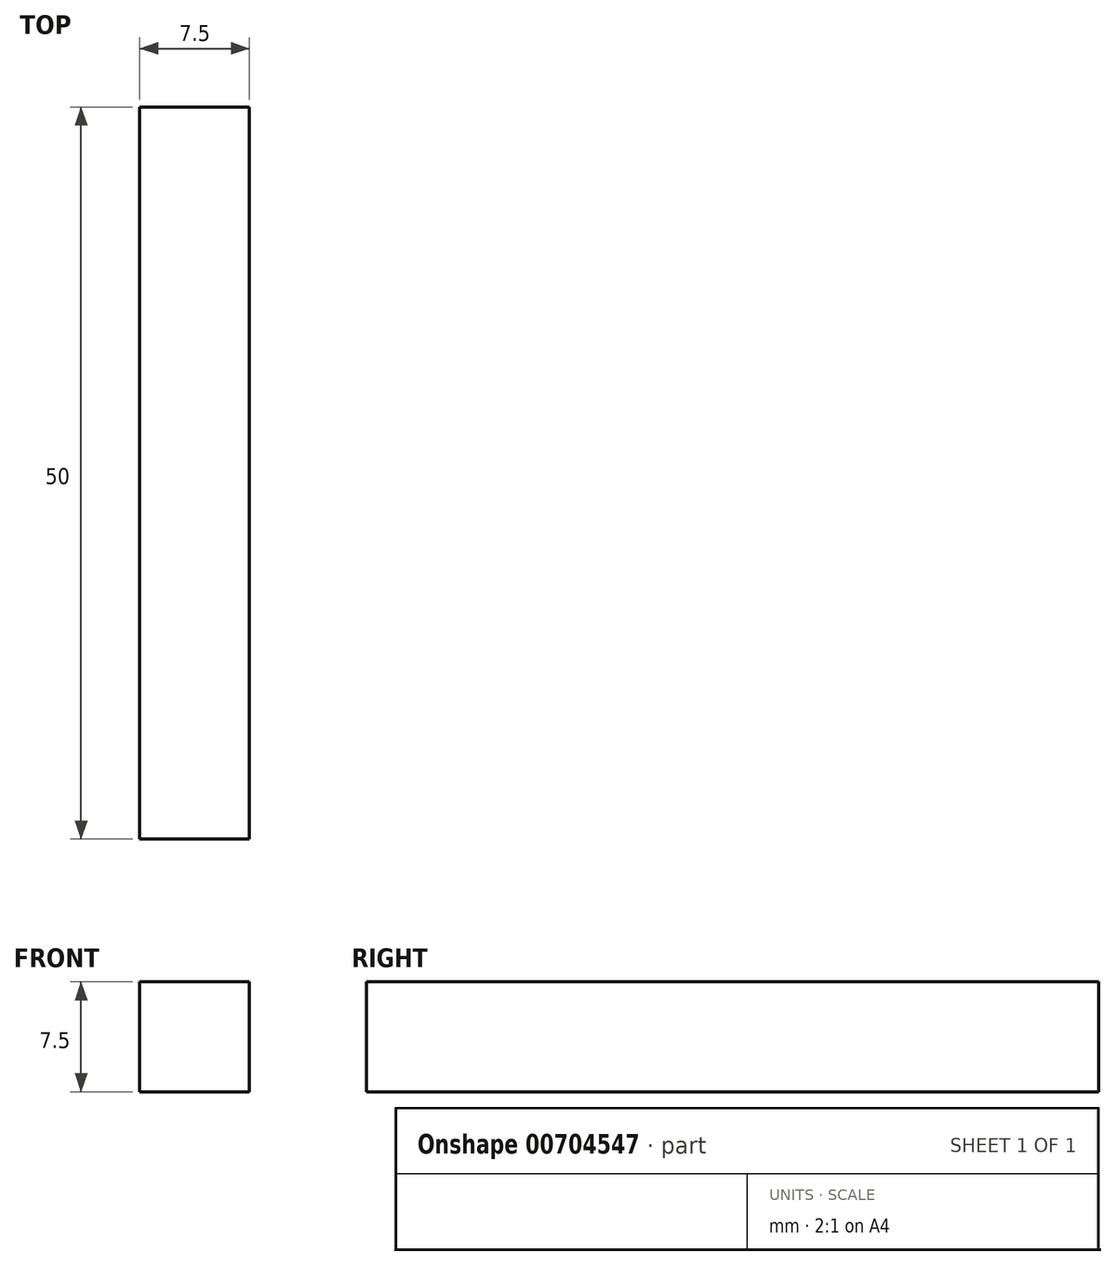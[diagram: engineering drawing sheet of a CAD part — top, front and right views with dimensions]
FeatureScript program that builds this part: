
annotation { "Feature Type Name" : "Feature", "Feature Type Description" : "" }
export const myFeature = defineFeature(function(context is Context, id is Id, definition is map)
    precondition{}
    {
        {
            var Q0;
            Q0=qCreatedBy(makeId("Front.planeOp"),FACE);
            var sketch = newSketch(context, id + "F0", { "sketchPlane" : qUnion([Q0])});
            skLineSegment(sketch, "E0.bottom", {"start": v(3.75, 3.75) * mm, "end": v(-3.75, 3.75) * mm});
            skLineSegment(sketch, "E0.top", {"start": v(3.75, -3.75) * mm, "end": v(-3.75, -3.75) * mm});
            skLineSegment(sketch, "E0.left", {"start": v(3.75, 3.75) * mm, "end": v(3.75, -3.75) * mm});
            skLineSegment(sketch, "E0.right", {"start": v(-3.75, 3.75) * mm, "end": v(-3.75, -3.75) * mm});
            skPoint(sketch, "E0.middle", {"position": v(0, 0) * mm});
            skSolve(sketch);
        }
        {
            var Q0;
            Q0 = qSketchRegion(id + "F0", true);
            extrude(context, id + "F1", {"entities" : qUnion([Q0]), "depth" : 50 * mm, "offsetDistance" : 25 * mm});
        }
    });
